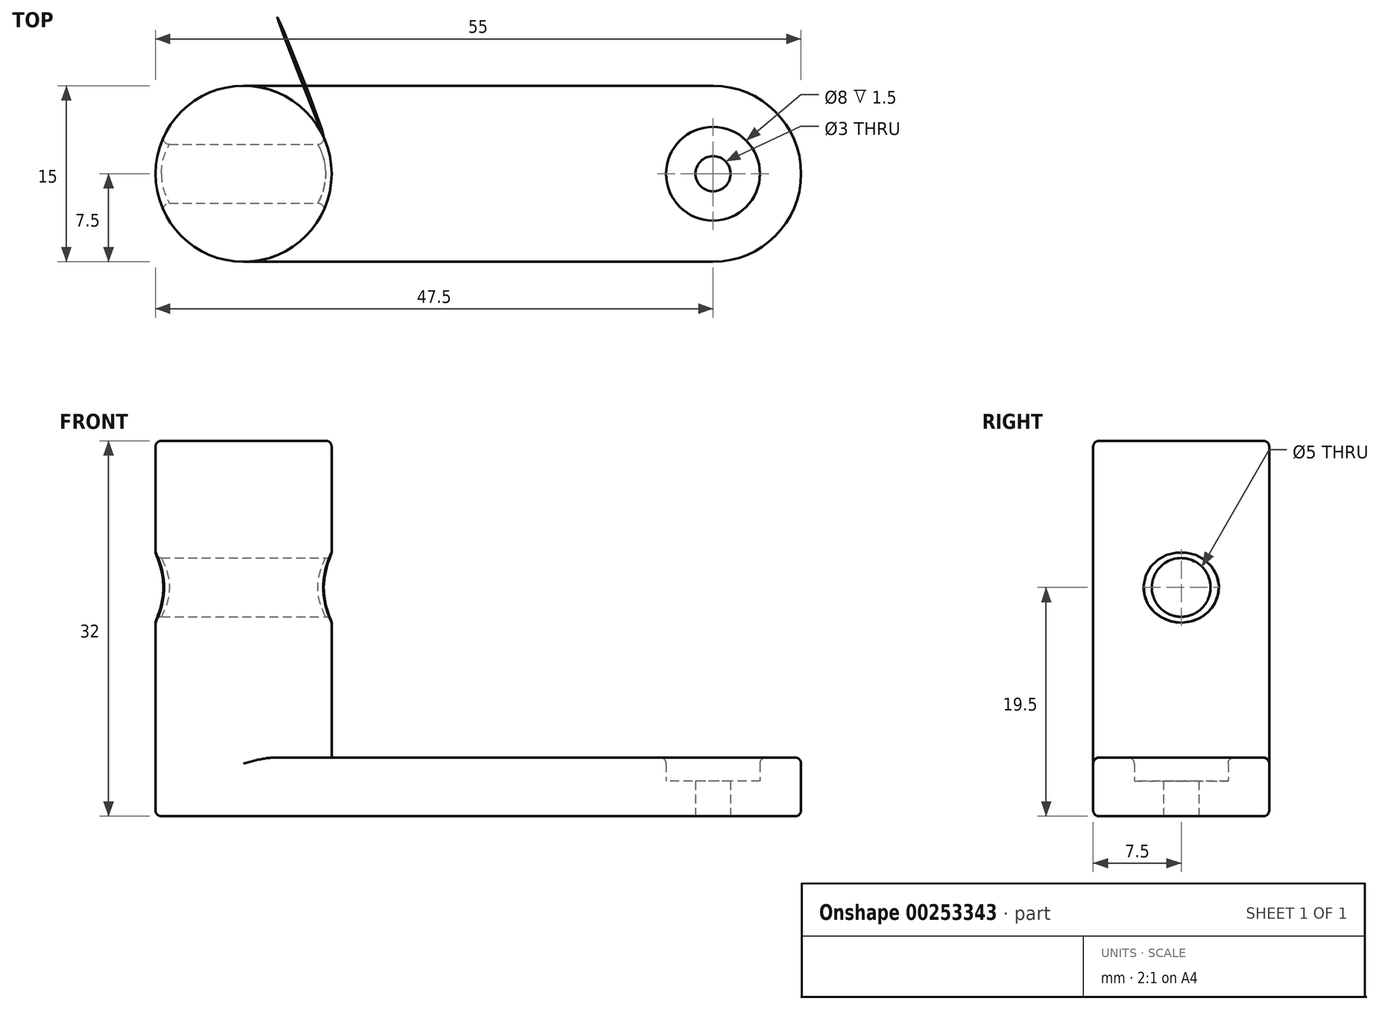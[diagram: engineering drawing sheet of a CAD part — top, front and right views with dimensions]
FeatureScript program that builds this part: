
annotation { "Feature Type Name" : "Feature", "Feature Type Description" : "" }
export const myFeature = defineFeature(function(context is Context, id is Id, definition is map)
    precondition{}
    {
        {
            var Q0;
            Q0=qCreatedBy(makeId("Top.planeOp"),FACE);
            var sketch = newSketch(context, id + "F0", { "sketchPlane" : qUnion([Q0])});
            skLineSegment(sketch, "E0.bottom", {"start": v(0, -7.5) * mm, "end": v(-55, -7.5) * mm});
            skLineSegment(sketch, "E0.top", {"start": v(0, 7.5) * mm, "end": v(-55, 7.5) * mm});
            skLineSegment(sketch, "E0.left", {"start": v(0, -7.5) * mm, "end": v(0, 7.5) * mm});
            skLineSegment(sketch, "E0.right", {"start": v(-55, -7.5) * mm, "end": v(-55, 7.5) * mm});
            skCircle(sketch, "E1", {"center": v(-47.5, 0) * mm, "radius": 7.5 * mm});
            skCircle(sketch, "E2", {"center": v(-7.5, 0) * mm, "radius": 1.5 * mm});
            skCircle(sketch, "E3", {"center": v(-7.5, 0) * mm, "radius": 4 * mm});
            skSolve(sketch);
        }
        {
            var Q0;
            {var subQ5=sQuery(id+"F0.wireOp",EDGE,"E0.left");Q0=makeQuery(id+"F0.imprint","IMPRINT",FACE,{"disambiguationData":[TD([[makeQuery(id+"F0.imprint","IMPRINT",EDGE,{"derivedFrom":subQ5}),1.0]])]});}
            extrude(context, id + "F1", {"entities" : qUnion([Q0]), "depth" : 5 * mm});
        }
        {
            var Q0;
            {var subQ0=sQuery(id+"F0.wireOp",EDGE,"E1");var subQ1=makeQuery(id+"F0.imprint","INTERSECT",VERTEX,{"derivedFrom":[sQuery(id+"F0.wireOp",EDGE,"E0.top"),subQ0]});Q0=makeQuery(id+"F0.imprint","IMPRINT",FACE,{"disambiguationData":[TD([[makeQuery(id+"F0.imprint","IMPRINT",EDGE,{"disambiguationData":[TD([[subQ1,-1.0]])],"derivedFrom":subQ0}),1.0]])]});}
            extrude(context, id + "F2", {"entities" : qUnion([Q0]), "operationType" : NewBodyOperationType.ADD, "depth" : 32 * mm});
        }
        {
            var Q0;
            Q0=makeQuery(id+"F0.imprint","IMPRINT",FACE,{"disambiguationData":[TD([[makeQuery(id+"F0.imprint","IMPRINT",EDGE,{"derivedFrom":sQuery(id+"F0.wireOp",EDGE,"E2")}),-1.0]])]});
            extrude(context, id + "F3", {"entities" : qUnion([Q0]), "operationType" : NewBodyOperationType.ADD, "depth" : 3 * mm});
        }
        {
            var Q0;
            Q0=makeQuery(id+"F1.opExtrude","SWEPT_EDGE",EDGE,{"disambiguationData":[OSD([sQuery(id+"F0.wireOp",EDGE,"E0.top"),sQuery(id+"F0.wireOp",EDGE,"E0.left")])]});
            var Q1;
            Q1=makeQuery(id+"F1.opExtrude","SWEPT_EDGE",EDGE,{"disambiguationData":[OSD([sQuery(id+"F0.wireOp",EDGE,"E0.bottom"),sQuery(id+"F0.wireOp",EDGE,"E0.left")])]});
            fillet(context, id + "F4", {"entities" : qUnion([Q0, Q1]), "radius" : 7.5 * mm, "tangentPropagation" : true, "allowEdgeOverflow" : false});
        }
        {
            var Q0;
            Q0=makeQuery(id+"F2.opExtrude","CAP_EDGE",EDGE,{"disambiguationData":[OSD([sQuery(id+"F0.wireOp",EDGE,"E1")])],"isStart":false});
            var Q1;
            Q1=makeQuery(id+"F1.opExtrude","CAP_EDGE",EDGE,{"disambiguationData":[OSD([sQuery(id+"F0.wireOp",EDGE,"E0.bottom")])],"isStart":false});
            var Q2;
            Q2=makeQuery(id+"F1.opExtrude","CAP_EDGE",EDGE,{"disambiguationData":[OSD([sQuery(id+"F0.wireOp",EDGE,"E0.top")])],"isStart":false});
            var Q3;
            Q3=makeQuery(id+"F1.opExtrude","CAP_EDGE",EDGE,{"disambiguationData":[OSD([sQuery(id+"F0.wireOp",EDGE,"E3")])],"isStart":false});
            var Q4;
            {var subQ0=sQuery(id+"F0.wireOp",EDGE,"E0.left");var subQ1=sQuery(id+"F0.wireOp",EDGE,"E0.top");Q4=makeQuery(id+"F4.opFillet","BLEND_EDGE",EDGE,{"blendedFrom":[makeQuery(id+"F1.opExtrude","SWEPT_EDGE",EDGE,{"disambiguationData":[OSD([subQ1,subQ0])]}),makeQuery(id+"F1.opExtrude","CAP_FACE",FACE,{"disambiguationData":[OSD([sQuery(id+"F0.wireOp",EDGE,"E0.bottom"),subQ1,subQ0,sQuery(id+"F0.wireOp",EDGE,"E1"),sQuery(id+"F0.wireOp",EDGE,"E3")])],"isStart":false})],"blendedInto":[makeQuery(id+"F1.opExtrude","CAP_FACE",FACE,{"disambiguationData":[OSD([sQuery(id+"F0.wireOp",EDGE,"E0.bottom"),subQ1,subQ0,sQuery(id+"F0.wireOp",EDGE,"E1"),sQuery(id+"F0.wireOp",EDGE,"E3")])],"isStart":false})]});}
            var Q5;
            Q5=makeQuery(id+"F1.opExtrude","CAP_EDGE",EDGE,{"disambiguationData":[OSD([sQuery(id+"F0.wireOp",EDGE,"E0.bottom")])],"isStart":true});
            fillet(context, id + "F5", {"entities" : qUnion([Q0, Q1, Q2, Q3, Q4, Q5]), "radius" : 0.5 * mm, "tangentPropagation" : true, "allowEdgeOverflow" : false});
        }
        {
            var Q0;
            Q0=qCreatedBy(makeId("Right.planeOp"),FACE);
            var sketch = newSketch(context, id + "F6", { "sketchPlane" : qUnion([Q0])});
            skCircle(sketch, "E4", {"center": v(0, 19.5) * mm, "radius": 2.5 * mm});
            skSolve(sketch);
        }
        {
            var Q0;
            Q0=makeQuery(id+"F6.imprint","IMPRINT",FACE,{"disambiguationData":[TD([[makeQuery(id+"F6.imprint","IMPRINT",EDGE,{"derivedFrom":sQuery(id+"F6.wireOp",EDGE,"E4")}),1.0]])]});
            extrude(context, id + "F7", {"entities" : qUnion([Q0]), "operationType" : NewBodyOperationType.REMOVE, "oppositeDirection" : true, "depth" : 60 * mm});
        }
        {
            var Q0;
            Q0=makeQuery(id+"F7.boolean.opBoolean","INTERSECT",EDGE,{"disambiguationData":[OD(0.0)],"derivedFrom":[makeQuery(id+"F2.opExtrude","SWEPT_FACE",FACE,{"disambiguationData":[OSD([sQuery(id+"F0.wireOp",EDGE,"E1")])]}),makeQuery(id+"F7.opExtrude","SWEPT_FACE",FACE,{"disambiguationData":[OSD([sQuery(id+"F6.wireOp",EDGE,"E4")])]})]});
            var Q1;
            Q1=makeQuery(id+"F7.boolean.opBoolean","INTERSECT",EDGE,{"disambiguationData":[OD(1.0)],"derivedFrom":[makeQuery(id+"F2.opExtrude","SWEPT_FACE",FACE,{"disambiguationData":[OSD([sQuery(id+"F0.wireOp",EDGE,"E1")])]}),makeQuery(id+"F7.opExtrude","SWEPT_FACE",FACE,{"disambiguationData":[OSD([sQuery(id+"F6.wireOp",EDGE,"E4")])]})]});
            fillet(context, id + "F8", {"entities" : qUnion([Q0, Q1]), "radius" : 0.5 * mm, "tangentPropagation" : true, "allowEdgeOverflow" : false});
        }
    });
